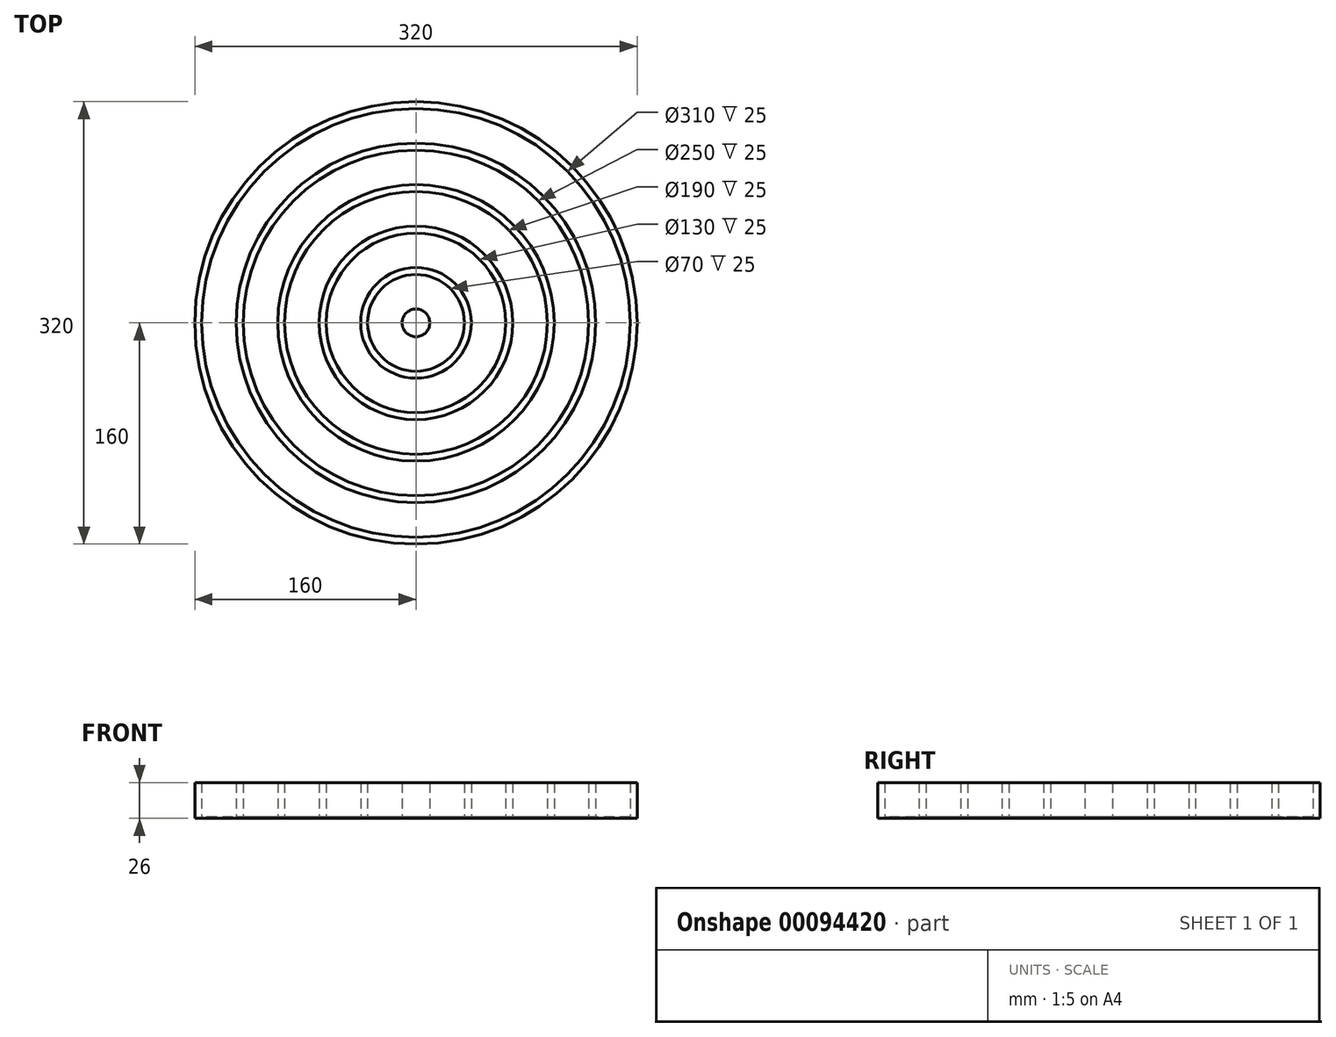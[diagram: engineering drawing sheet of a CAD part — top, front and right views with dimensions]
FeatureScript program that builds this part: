
annotation { "Feature Type Name" : "Feature", "Feature Type Description" : "" }
export const myFeature = defineFeature(function(context is Context, id is Id, definition is map)
    precondition{}
    {
        {
            var Q0;
            Q0=qCreatedBy(makeId("Top.planeOp"),FACE);
            var sketch = newSketch(context, id + "F0", { "sketchPlane" : qUnion([Q0])});
            skCircle(sketch, "E0", {"center": v(0, 0) * mm, "radius": 160 * mm});
            skSolve(sketch);
        }
        {
            var Q0;
            Q0=makeQuery(id+"F0.imprint","IMPRINT",FACE,{"disambiguationData":[TD([[makeQuery(id+"F0.imprint","IMPRINT",EDGE,{"derivedFrom":sQuery(id+"F0.wireOp",EDGE,"E0")}),1.0]])]});
            extrude(context, id + "F1", {"entities" : qUnion([Q0]), "oppositeDirection" : true, "depth" : 1 * mm});
        }
        {
            var Q0;
            Q0=makeQuery(id+"F1.opExtrude","CAP_FACE",FACE,{"disambiguationData":[OSD([sQuery(id+"F0.wireOp",EDGE,"E0")])],"isStart":true});
            var sketch = newSketch(context, id + "F2", { "sketchPlane" : qUnion([Q0])});
            skCircle(sketch, "E1", {"center": v(0, 0) * mm, "radius": 160 * mm});
            skCircle(sketch, "E2", {"center": v(0, 0) * mm, "radius": 155 * mm});
            skCircle(sketch, "E3", {"center": v(0, 0) * mm, "radius": 130 * mm});
            skCircle(sketch, "E4", {"center": v(0, 0) * mm, "radius": 125 * mm});
            skCircle(sketch, "E5", {"center": v(0, 0) * mm, "radius": 100 * mm});
            skCircle(sketch, "E6", {"center": v(0, 0) * mm, "radius": 95 * mm});
            skCircle(sketch, "E7", {"center": v(0, 0) * mm, "radius": 70 * mm});
            skCircle(sketch, "E8", {"center": v(0, 0) * mm, "radius": 65 * mm});
            skCircle(sketch, "E9", {"center": v(0, 0) * mm, "radius": 40 * mm});
            skCircle(sketch, "E10", {"center": v(0, 0) * mm, "radius": 35 * mm});
            skCircle(sketch, "E11", {"center": v(0, 0) * mm, "radius": 10 * mm});
            skSolve(sketch);
        }
        {
            var Q0;
            Q0=makeQuery(id+"F2.imprint","IMPRINT",FACE,{"disambiguationData":[TD([[makeQuery(id+"F2.imprint","IMPRINT",EDGE,{"derivedFrom":sQuery(id+"F2.wireOp",EDGE,"E1")}),1.0]])]});
            var Q1;
            Q1=makeQuery(id+"F2.imprint","IMPRINT",FACE,{"disambiguationData":[TD([[makeQuery(id+"F2.imprint","IMPRINT",EDGE,{"derivedFrom":sQuery(id+"F2.wireOp",EDGE,"E3")}),1.0]])]});
            var Q2;
            Q2=makeQuery(id+"F2.imprint","IMPRINT",FACE,{"disambiguationData":[TD([[makeQuery(id+"F2.imprint","IMPRINT",EDGE,{"derivedFrom":sQuery(id+"F2.wireOp",EDGE,"E5")}),1.0]])]});
            var Q3;
            Q3=makeQuery(id+"F2.imprint","IMPRINT",FACE,{"disambiguationData":[TD([[makeQuery(id+"F2.imprint","IMPRINT",EDGE,{"derivedFrom":sQuery(id+"F2.wireOp",EDGE,"E7")}),1.0]])]});
            var Q4;
            Q4=makeQuery(id+"F2.imprint","IMPRINT",FACE,{"disambiguationData":[TD([[makeQuery(id+"F2.imprint","IMPRINT",EDGE,{"derivedFrom":sQuery(id+"F2.wireOp",EDGE,"E9")}),1.0]])]});
            var Q5;
            Q5=makeQuery(id+"F2.imprint","IMPRINT",FACE,{"disambiguationData":[TD([[makeQuery(id+"F2.imprint","IMPRINT",EDGE,{"derivedFrom":sQuery(id+"F2.wireOp",EDGE,"E11")}),1.0]])]});
            extrude(context, id + "F3", {"entities" : qUnion([Q0, Q1, Q2, Q3, Q4, Q5]), "operationType" : NewBodyOperationType.ADD, "depth" : 25 * mm});
        }
    });
